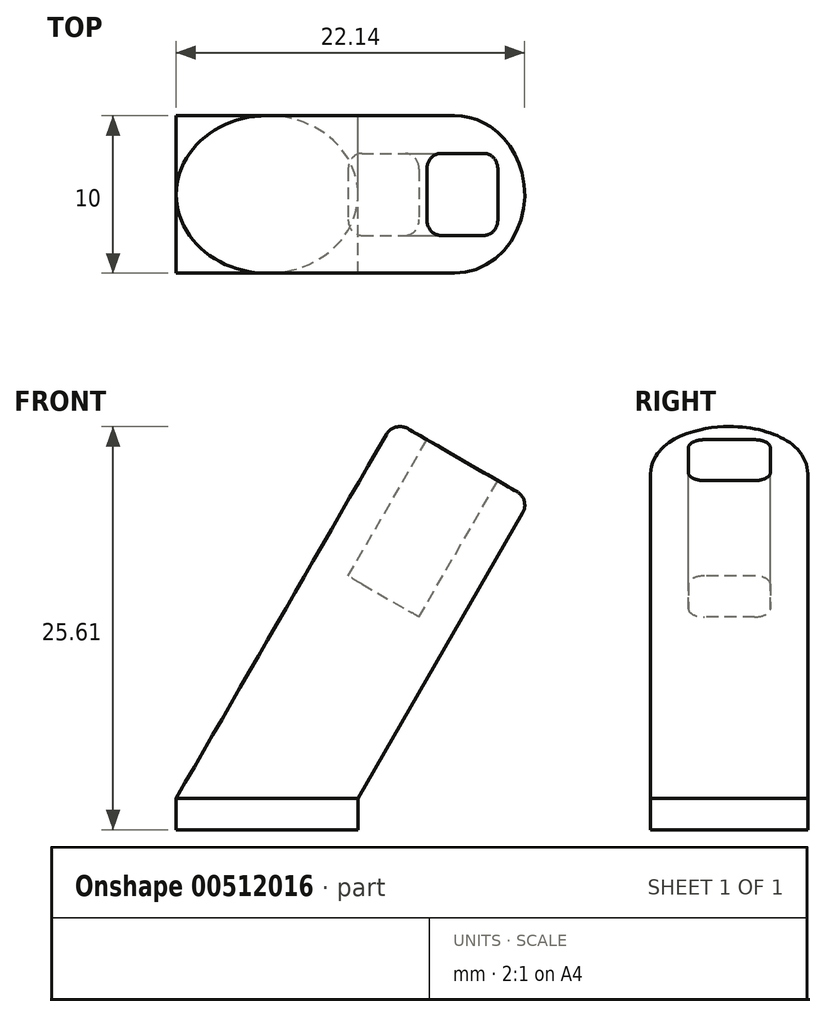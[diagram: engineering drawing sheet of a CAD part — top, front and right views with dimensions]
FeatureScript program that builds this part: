
annotation { "Feature Type Name" : "Feature", "Feature Type Description" : "" }
export const myFeature = defineFeature(function(context is Context, id is Id, definition is map)
    precondition{}
    {
        {
            var Q0;
            Q0=qCreatedBy(makeId("Front.planeOp"),FACE);
            var sketch = newSketch(context, id + "F0", { "sketchPlane" : qUnion([Q0])});
            skLineSegment(sketch, "E0", {"start": v(0, 0) * mm, "end": v(8.66, -5) * mm});
            skSolve(sketch);
        }
        {
            var Q0;
            Q0 = qSketchRegion(id + "F0", true);
            var Q1;
            Q1=sQuery(id+"F0.wireOp",EDGE,"E0");
            extrude(context, id + "F1", {"entities" : qUnion([Q0]), "bodyType" : ExtendedToolBodyType.SURFACE, "surfaceEntities" : qUnion([Q1]), "depth" : 10 * mm, "offsetDistance" : 25 * mm, "symmetric" : true});
        }
        {
            var Q0;
            Q0=makeQuery(id+"F1.opExtrude","SWEPT_FACE",FACE,{"disambiguationData":[OSD([sQuery(id+"F0.wireOp",EDGE,"E0")])]});
            var sketch = newSketch(context, id + "F2", { "sketchPlane" : qUnion([Q0])});
            skCircle(sketch, "E1", {"center": v(5, 0) * mm, "radius": 5 * mm});
            skPoint(sketch, "E1.first.point", {"position": v(0, 0) * mm});
            skPoint(sketch, "E1.second.point", {"position": v(5, -5) * mm});
            skPoint(sketch, "E1.third.point", {"position": v(10, 0) * mm});
            skSolve(sketch);
        }
        {
            var Q0;
            Q0 = qSketchRegion(id + "F2", true);
            extrude(context, id + "F3", {"entities" : qUnion([Q0]), "oppositeDirection" : true, "depth" : 30 * mm, "offsetDistance" : 25 * mm});
        }
        {
            var Q0;
            Q0=qCreatedBy(makeId("Front.planeOp"),FACE);
            var sketch = newSketch(context, id + "F4", { "sketchPlane" : qUnion([Q0])});
            skLineSegment(sketch, "E2.bottom", {"start": v(0, 2) * mm, "end": v(12.7, 2) * mm});
            skLineSegment(sketch, "E2.top", {"start": v(0, -5) * mm, "end": v(12.7, -5) * mm});
            skLineSegment(sketch, "E2.left", {"start": v(0, 2) * mm, "end": v(0, -5) * mm});
            skLineSegment(sketch, "E2.right", {"start": v(12.7, 2) * mm, "end": v(12.7, -5) * mm});
            skLineSegment(sketch, "E3", {"start": v(18.66, 12.32) * mm, "end": v(8.66, -5) * mm, "construction": true});
            skPoint(sketch, "E4.0", {"position": v(8.66, -5) * mm});
            skSolve(sketch);
        }
        {
            var Q0;
            Q0 = qSketchRegion(id + "F4", true);
            extrude(context, id + "F5", {"entities" : qUnion([Q0]), "operationType" : NewBodyOperationType.REMOVE, "depth" : 11 * mm, "offsetDistance" : 25 * mm, "symmetric" : true});
        }
        {
            var Q0;
            Q0=makeQuery(id+"F5.boolean.opBoolean","COPY",FACE,{"derivedFrom":makeQuery(id+"F5.opExtrude","SWEPT_FACE",FACE,{"disambiguationData":[OSD([sQuery(id+"F4.wireOp",EDGE,"E2.bottom")])]})});
            var sketch = newSketch(context, id + "F6", { "sketchPlane" : qUnion([Q0])});
            skEllipse(sketch, "E5.0", {"center": v(6.93, 0) * mm, "majorRadius": 5.77 * mm, "minorRadius": 5 * mm, "majorAxis": v(-1, 0), "construction": true});
            skPoint(sketch, "E6.firstSnap0", {"position": v(6.93, 5) * mm});
            skPoint(sketch, "E6.firstSnap1", {"position": v(1.15, 0) * mm});
            skPoint(sketch, "E6.oppositeSnap0", {"position": v(6.93, -5) * mm});
            skPoint(sketch, "E6.oppositeSnap1", {"position": v(12.7, 0) * mm});
            skLineSegment(sketch, "E6.bottom", {"start": v(1.15, 5) * mm, "end": v(12.7, 5) * mm});
            skLineSegment(sketch, "E6.top", {"start": v(1.15, -5) * mm, "end": v(12.7, -5) * mm});
            skLineSegment(sketch, "E6.left", {"start": v(1.15, 5) * mm, "end": v(1.15, -5) * mm});
            skLineSegment(sketch, "E6.right", {"start": v(12.7, 5) * mm, "end": v(12.7, -5) * mm});
            skSolve(sketch);
        }
        {
            var Q0;
            Q0 = qSketchRegion(id + "F6", true);
            extrude(context, id + "F7", {"entities" : qUnion([Q0]), "operationType" : NewBodyOperationType.ADD, "depth" : 2 * mm, "offsetDistance" : 25 * mm});
        }
        {
            var Q0;
            Q0=makeQuery(id+"F3.opExtrude","CAP_FACE",FACE,{"disambiguationData":[OSD([sQuery(id+"F2.wireOp",EDGE,"E1")])],"isStart":false});
            var sketch = newSketch(context, id + "F8", { "sketchPlane" : qUnion([Q0])});
            skCircle(sketch, "E7.0", {"center": v(5, 0) * mm, "radius": 5 * mm, "construction": true});
            skLineSegment(sketch, "E8.bottom", {"start": v(3.4, 2.6) * mm, "end": v(6.6, 2.6) * mm});
            skLineSegment(sketch, "E8.top", {"start": v(3.4, -2.6) * mm, "end": v(6.6, -2.6) * mm});
            skLineSegment(sketch, "E8.left", {"start": v(2.4, 1.6) * mm, "end": v(2.4, -1.6) * mm});
            skLineSegment(sketch, "E8.right", {"start": v(7.6, 1.6) * mm, "end": v(7.6, -1.6) * mm});
            skPoint(sketch, "E9.visualSharp", {"position": v(2.4, 2.6) * mm});
            skArc(sketch, "E9.filletArc", {"start": v(3.4, 2.6) * mm, "mid": v(2.7, 2.3) * mm, "end": v(2.4, 1.6) * mm});
            skPoint(sketch, "E10.visualSharp", {"position": v(7.6, 2.6) * mm});
            skArc(sketch, "E10.filletArc", {"start": v(7.6, 1.6) * mm, "mid": v(7.3, 2.3) * mm, "end": v(6.6, 2.6) * mm});
            skPoint(sketch, "E11.visualSharp", {"position": v(7.6, -2.6) * mm});
            skArc(sketch, "E11.filletArc", {"start": v(6.6, -2.6) * mm, "mid": v(7.3, -2.3) * mm, "end": v(7.6, -1.6) * mm});
            skPoint(sketch, "E12.visualSharp", {"position": v(2.4, -2.6) * mm});
            skArc(sketch, "E12.filletArc", {"start": v(2.4, -1.6) * mm, "mid": v(2.7, -2.3) * mm, "end": v(3.4, -2.6) * mm});
            skSolve(sketch);
        }
        {
            var Q0;
            Q0 = qSketchRegion(id + "F8", true);
            extrude(context, id + "F9", {"entities" : qUnion([Q0]), "operationType" : NewBodyOperationType.REMOVE, "oppositeDirection" : true, "depth" : 10 * mm, "offsetDistance" : 25 * mm});
        }
        {
            var Q0;
            Q0=makeQuery(id+"F3.opExtrude","CAP_EDGE",EDGE,{"disambiguationData":[OSD([sQuery(id+"F2.wireOp",EDGE,"E1")])],"isStart":false});
            fillet(context, id + "F10", {"entities" : qUnion([Q0]), "radius" : 1 * mm, "tangentPropagation" : true, "allowEdgeOverflow" : false});
        }
    });
